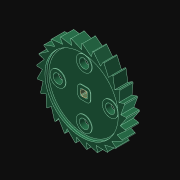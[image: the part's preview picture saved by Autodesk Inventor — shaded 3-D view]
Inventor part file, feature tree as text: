
AUTODESK INVENTOR PART (.ipt)
format: ipt  version: 2021.3 (Build 253353010, 353A)  size: 415,232 bytes
history: native  units: in
note: dims shown in document units (in); Inventor stores cm internally (conversion verified against a paired STEP export)
features: imported_body x2, sketch x1, other x1, extrude x1
ambient origin geometry x8: Origin, YZ Plane, XZ Plane, XY Plane, X Axis, Y Axis, Z Axis, Center Point
bodies: Body1 (feature_tree), Body2 (feature_tree)
feature tree (5):
  imported_body  "Imported1"
  imported_body  "Base1"
  sketch  "Sketch1"  dims[d0=1.0in d1=0.0in]
  other  "Srf1"
  extrude  "ExtrusionSrf1"  [1 undecoded]
note: 1 required parameter value undecoded (feature->parameter linkage not recoverable at this tier; creation-order binding heuristic only, values carry confidence <= 0.55)
